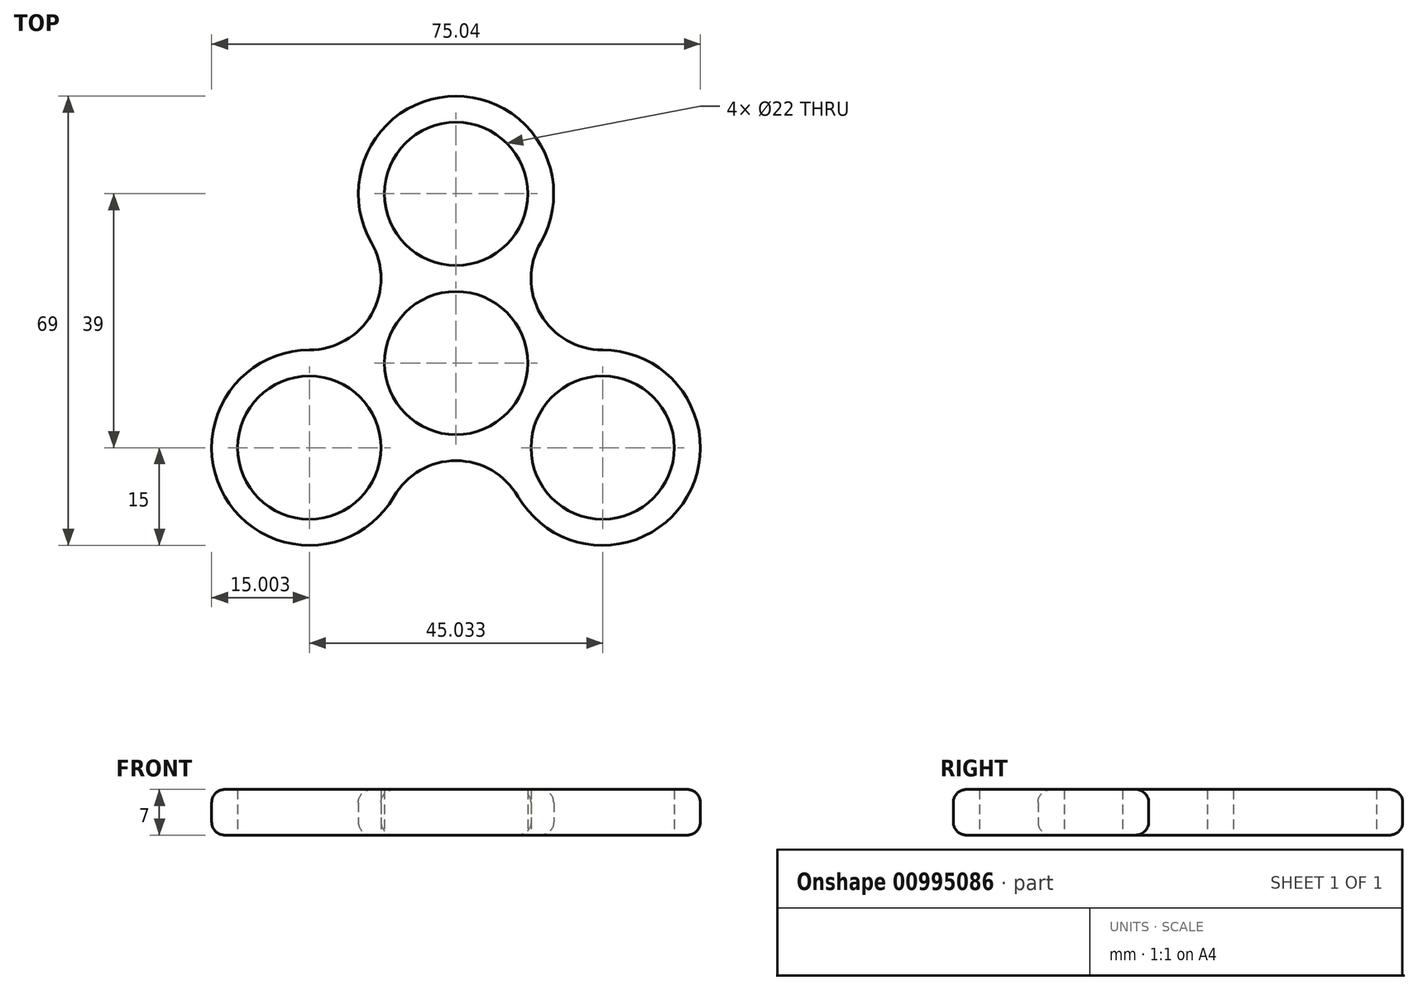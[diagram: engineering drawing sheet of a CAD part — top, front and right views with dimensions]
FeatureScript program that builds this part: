
annotation { "Feature Type Name" : "Feature", "Feature Type Description" : "" }
export const myFeature = defineFeature(function(context is Context, id is Id, definition is map)
    precondition{}
    {
        {
            var Q0;
            Q0=qCreatedBy(makeId("Top.planeOp"),FACE);
            var sketch = newSketch(context, id + "F0", { "sketchPlane" : qUnion([Q0])});
            skCircle(sketch, "E0", {"center": v(0, 0) * mm, "radius": 11 * mm});
            skCircle(sketch, "E1", {"center": v(0, 26) * mm, "radius": 11 * mm});
            skCircle(sketch, "E2.1.0", {"center": v(-22.52, -13) * mm, "radius": 11 * mm});
            skCircle(sketch, "E2.2.0", {"center": v(22.52, -13) * mm, "radius": 11 * mm});
            skCircle(sketch, "E3", {"center": v(0, 26) * mm, "radius": 15 * mm});
            skCircle(sketch, "E4.1.0", {"center": v(-22.52, -13) * mm, "radius": 15 * mm});
            skCircle(sketch, "E4.2.0", {"center": v(22.52, -13) * mm, "radius": 15 * mm});
            skArc(sketch, "E5", {"start": v(-22.52, 2) * mm, "mid": v(-13, 7.5) * mm, "end": v(-13, 18.5) * mm});
            skArc(sketch, "E6", {"start": v(13, 18.5) * mm, "mid": v(13, 7.5) * mm, "end": v(22.52, 2) * mm});
            skArc(sketch, "E7", {"start": v(9.53, -20.5) * mm, "mid": v(0, -15) * mm, "end": v(-9.53, -20.5) * mm});
            skSolve(sketch);
        }
        {
            var Q0;
            Q0 = qSketchRegion(id + "F0", true);
            extrude(context, id + "F1", {"entities" : qUnion([Q0]), "depth" : 7 * mm, "offsetDistance" : 25 * mm});
        }
        {
            var Q0;
            Q0=makeQuery(id+"F1.opExtrude","SWEPT_FACE",FACE,{"disambiguationData":[OSD([sQuery(id+"F0.wireOp",EDGE,"E4.1.0")])]});
            fillet(context, id + "F2", {"entities" : qUnion([Q0]), "radius" : 2 * mm, "tangentPropagation" : true, "allowEdgeOverflow" : false});
        }
    });
